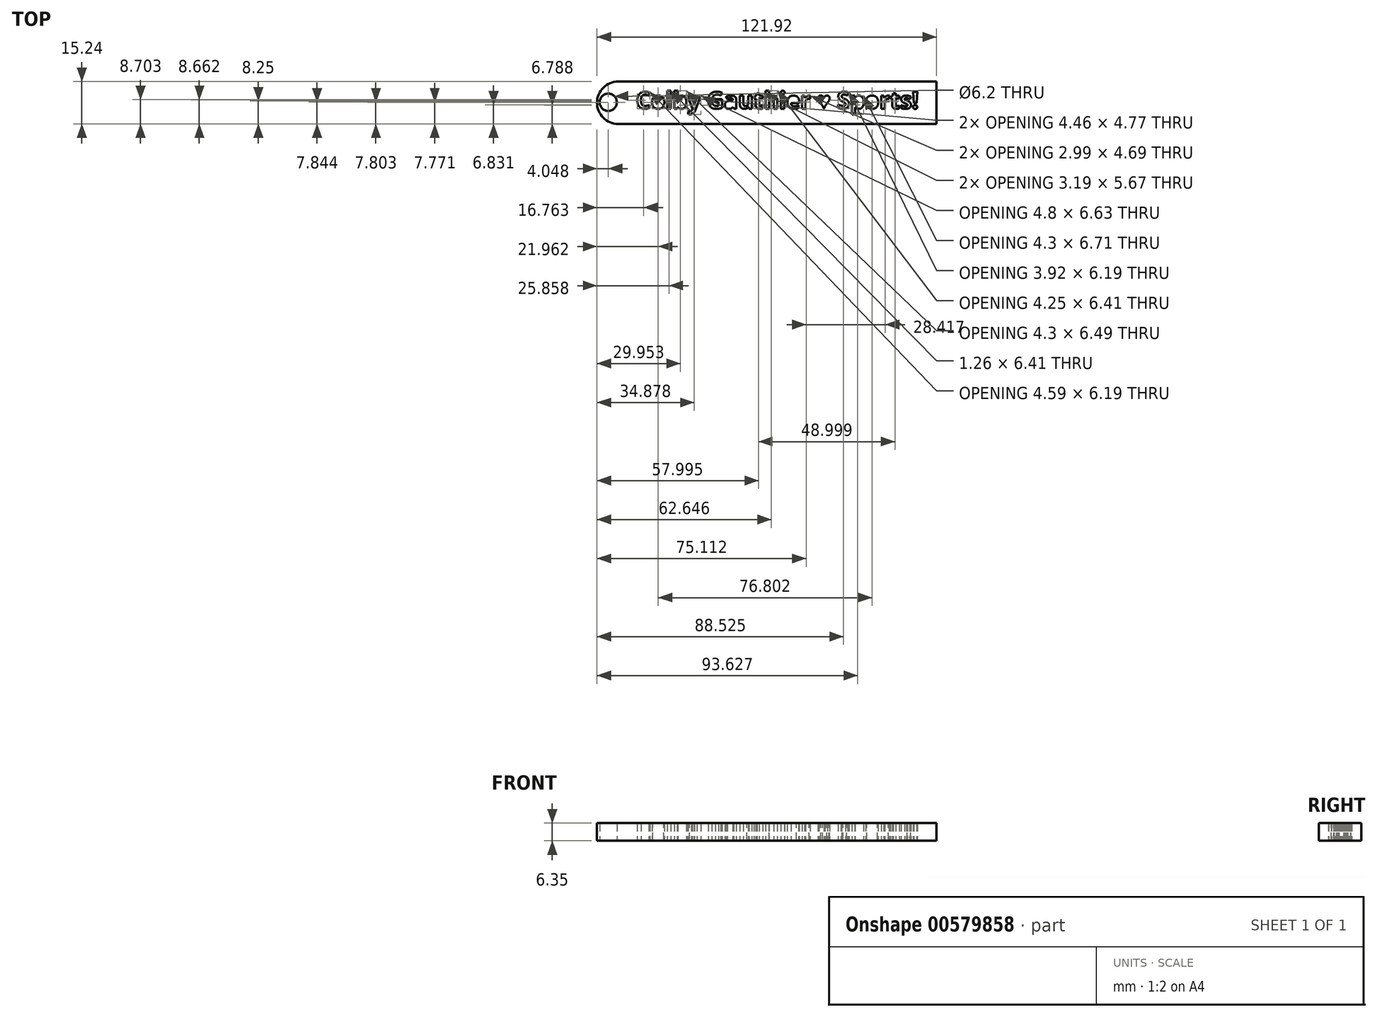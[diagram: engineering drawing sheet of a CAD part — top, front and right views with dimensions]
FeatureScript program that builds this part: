
annotation { "Feature Type Name" : "Feature", "Feature Type Description" : "" }
export const myFeature = defineFeature(function(context is Context, id is Id, definition is map)
    precondition{}
    {
        {
            var Q0;
            Q0=qCreatedBy(makeId("Top.planeOp"),FACE);
            var sketch = newSketch(context, id + "F0", { "sketchPlane" : qUnion([Q0])});
            skText(sketch, "E0", { "text": "Colby Gauthier ♥ Sports!", "fontName": "NotoSans-Bold.ttf"});
            skLineSegment(sketch, "E1.bottom", {"start": v(96.44, -4.32) * mm, "end": v(-17.86, -4.32) * mm});
            skLineSegment(sketch, "E1.top", {"start": v(96.44, 10.92) * mm, "end": v(-17.86, 10.92) * mm});
            skLineSegment(sketch, "E1.left", {"start": v(96.44, -4.32) * mm, "end": v(96.44, 10.92) * mm});
            skLineSegment(sketch, "E1.right", {"start": v(-17.86, -4.32) * mm, "end": v(-17.86, 10.92) * mm});
            skPoint(sketch, "E1.middle", {"position": v(39.3, 3.3) * mm});
            skPoint(sketch, "E1.middle.positionSnap0", {"position": v(39.3, 4.22) * mm});
            skPoint(sketch, "E1.centerSnap0", {"position": v(39.3, 4.22) * mm});
            skArc(sketch, "E2", {"start": v(-17.86, 10.92) * mm, "mid": v(-25.48, 3.3) * mm, "end": v(-17.86, -4.32) * mm});
            skCircle(sketch, "E3", {"center": v(-21.43, 3.45) * mm, "radius": 3.1 * mm});
            const initialGuessF0  = {"E0": [-0.0115, 0.00118, 1, 0, 0.00607]};
            skSetInitialGuess(sketch, initialGuessF0);
            skSolve(sketch);
        }
        {
            var Q0;
            Q0 = qSketchRegion(id + "F0", true);
            extrude(context, id + "F1", {"entities" : qUnion([Q0]), "depth" : 6.35 * mm, "offsetDistance" : 25.4 * mm});
        }
    });
